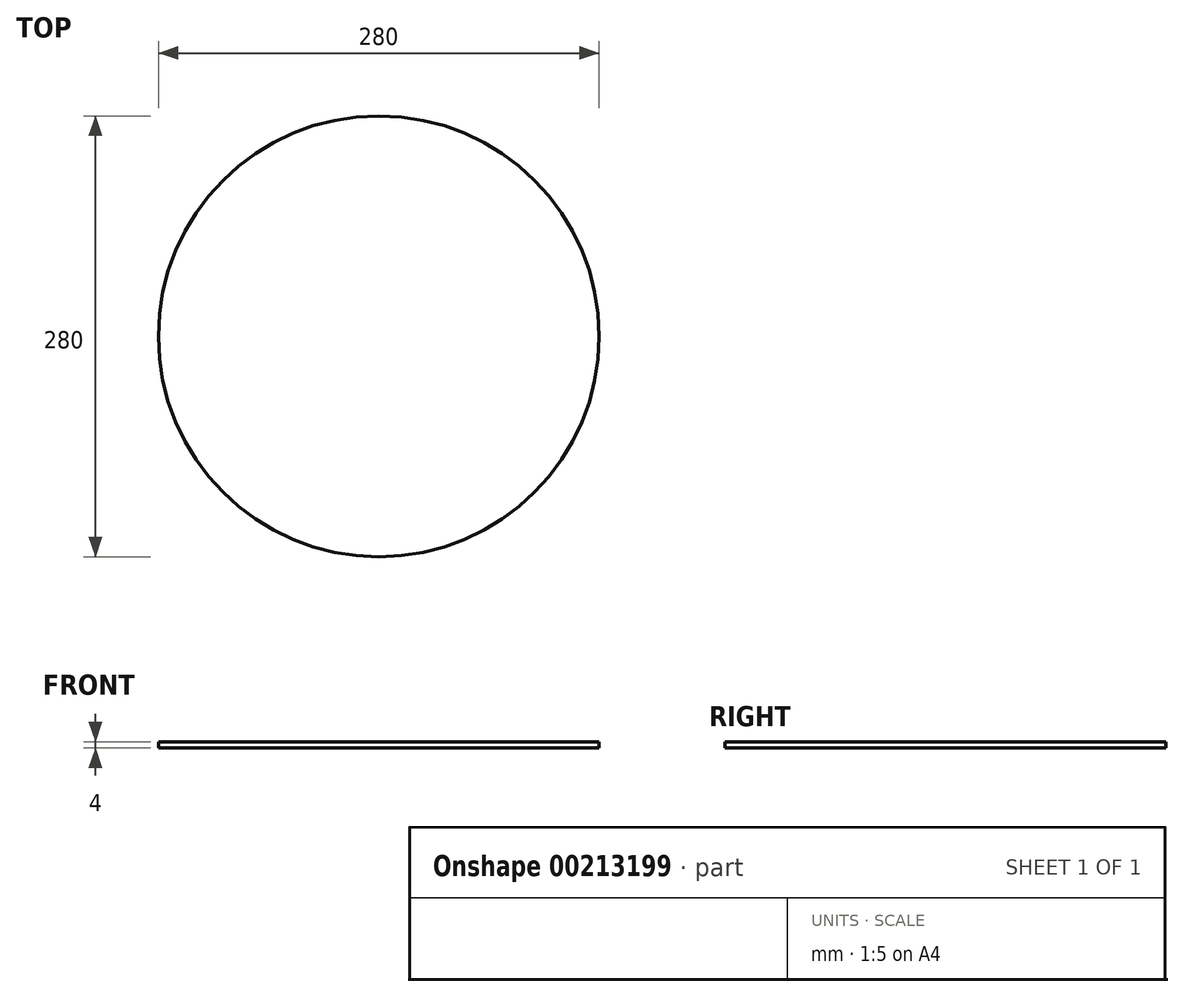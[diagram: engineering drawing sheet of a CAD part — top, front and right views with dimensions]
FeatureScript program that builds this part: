
annotation { "Feature Type Name" : "Feature", "Feature Type Description" : "" }
export const myFeature = defineFeature(function(context is Context, id is Id, definition is map)
    precondition{}
    {
        {
            var Q0;
            Q0=qCreatedBy(makeId("Top.planeOp"),FACE);
            var sketch = newSketch(context, id + "F0", { "sketchPlane" : qUnion([Q0])});
            skCircle(sketch, "E0", {"center": v(0, 0) * mm, "radius": 140 * mm});
            skSolve(sketch);
        }
        {
            var Q0;
            Q0=makeQuery(id+"F0.imprint","IMPRINT",FACE,{"disambiguationData":[TD([[makeQuery(id+"F0.imprint","IMPRINT",EDGE,{"derivedFrom":sQuery(id+"F0.wireOp",EDGE,"E0")}),1.0]])]});
            extrude(context, id + "F1", {"entities" : qUnion([Q0]), "depth" : 4 * mm});
        }
    });
